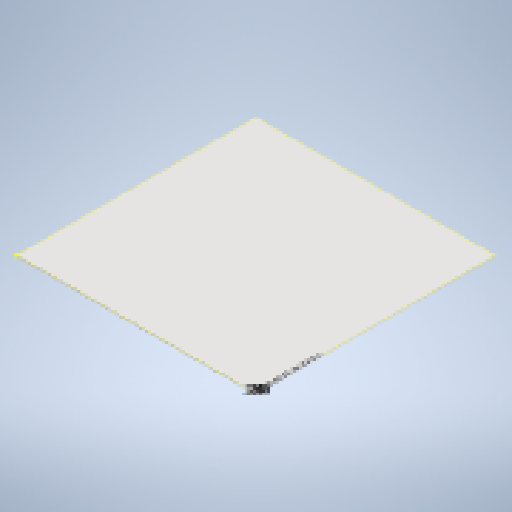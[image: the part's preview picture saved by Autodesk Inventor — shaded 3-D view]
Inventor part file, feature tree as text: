
AUTODESK INVENTOR PART (.ipt)
format: ipt  version: 2025 (Build 290162000, 162)  size: 244,224 bytes
history: native  units: in
note: dims shown in document units (in); Inventor stores cm internally (conversion verified against a paired STEP export)
features: extrude x3, sketch x3, projected_geometry x2
ambient origin geometry x8: Origin, YZ Plane, XZ Plane, XY Plane, X Axis, Y Axis, Z Axis, Center Point
bodies: Solid1 (feature_tree), Solid2 (feature_tree)
feature tree (8):
  extrude  "Extrusion1"  Depth=9.0in
  extrude  "Extrusion2"  Depth=0.1181in
  extrude  "Extrusion3"  Depth=2.75in TaperAngle=0.0deg
  sketch  "Sketch1"  dims[d0=6.0in d1=9.0in]
  sketch  "Sketch3"  dims[d2=0.0787in d3=0.0in d13=0.1181in]
  projected_geometry  "Projected Loop2"
  sketch  "Sketch4"  dims[d14=0.1in d15=0.0in d16=2.75in d17=0.0in]
  projected_geometry  "Projected Loop3"
